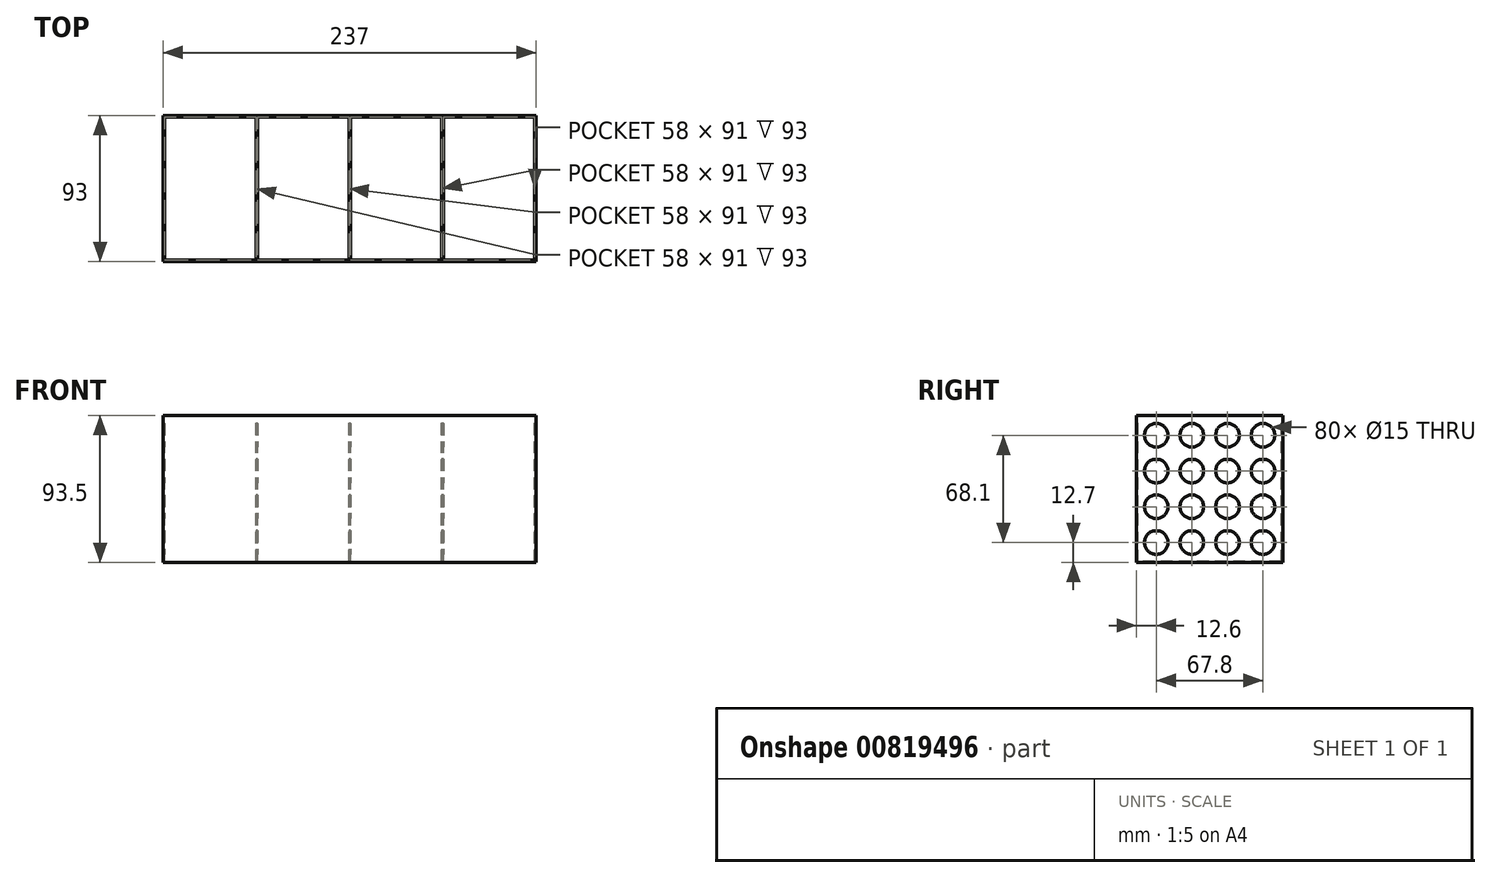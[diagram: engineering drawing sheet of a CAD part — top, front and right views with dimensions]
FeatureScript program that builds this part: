
annotation { "Feature Type Name" : "Feature", "Feature Type Description" : "" }
export const myFeature = defineFeature(function(context is Context, id is Id, definition is map)
    precondition{}
    {
        {
            var Q0;
            Q0=qCreatedBy(makeId("Top.planeOp"),FACE);
            var sketch = newSketch(context, id + "F0", { "sketchPlane" : qUnion([Q0])});
            skLineSegment(sketch, "E0.bottom", {"start": v(-118.5, 46.5) * mm, "end": v(118.5, 46.5) * mm});
            skLineSegment(sketch, "E0.top", {"start": v(-118.5, -46.5) * mm, "end": v(118.5, -46.5) * mm});
            skLineSegment(sketch, "E0.left", {"start": v(-118.5, 46.5) * mm, "end": v(-118.5, -46.5) * mm});
            skLineSegment(sketch, "E0.right", {"start": v(118.5, 46.5) * mm, "end": v(118.5, -46.5) * mm});
            skPoint(sketch, "E0.middle", {"position": v(0, 0) * mm});
            skSolve(sketch);
        }
        {
            var Q0;
            Q0=makeQuery(id+"F0.imprint","IMPRINT",FACE,{"disambiguationData":[TD([[makeQuery(id+"F0.imprint","IMPRINT",EDGE,{"derivedFrom":sQuery(id+"F0.wireOp",EDGE,"E0.bottom")}),-1.0]])]});
            extrude(context, id + "F1", {"entities" : qUnion([Q0]), "depth" : 93.5 * mm, "offsetDistance" : 25 * mm});
        }
        {
            var Q0;
            Q0=makeQuery(id+"F1.opExtrude","CAP_FACE",FACE,{"disambiguationData":[OSD([sQuery(id+"F0.wireOp",EDGE,"E0.bottom"),sQuery(id+"F0.wireOp",EDGE,"E0.top"),sQuery(id+"F0.wireOp",EDGE,"E0.left"),sQuery(id+"F0.wireOp",EDGE,"E0.right")])],"isStart":false});
            var sketch = newSketch(context, id + "F2", { "sketchPlane" : qUnion([Q0])});
            skLineSegment(sketch, "E1.bottom", {"start": v(-117.5, 45.5) * mm, "end": v(-59.5, 45.5) * mm});
            skLineSegment(sketch, "E1.top", {"start": v(-117.5, -45.5) * mm, "end": v(-59.5, -45.5) * mm});
            skLineSegment(sketch, "E1.left", {"start": v(-117.5, 45.5) * mm, "end": v(-117.5, -45.5) * mm});
            skLineSegment(sketch, "E1.right", {"start": v(-59.5, 45.5) * mm, "end": v(-59.5, -45.5) * mm});
            skLineSegment(sketch, "E2", {"start": v(-59.5, 45.5) * mm, "end": v(-58.5, 45.5) * mm});
            skLineSegment(sketch, "E3.bottom", {"start": v(-58.5, 45.5) * mm, "end": v(-0.5, 45.5) * mm});
            skLineSegment(sketch, "E3.top", {"start": v(-58.5, -45.5) * mm, "end": v(-0.5, -45.5) * mm});
            skLineSegment(sketch, "E3.left", {"start": v(-58.5, 45.5) * mm, "end": v(-58.5, -45.5) * mm});
            skLineSegment(sketch, "E3.right", {"start": v(-0.5, 45.5) * mm, "end": v(-0.5, -45.5) * mm});
            skLineSegment(sketch, "E4", {"start": v(-0.5, 45.5) * mm, "end": v(0.5, 45.5) * mm});
            skLineSegment(sketch, "E5.bottom", {"start": v(0.5, 45.5) * mm, "end": v(58.5, 45.5) * mm});
            skLineSegment(sketch, "E5.top", {"start": v(0.5, -45.5) * mm, "end": v(58.5, -45.5) * mm});
            skLineSegment(sketch, "E5.left", {"start": v(0.5, 45.5) * mm, "end": v(0.5, -45.5) * mm});
            skLineSegment(sketch, "E5.right", {"start": v(58.5, 45.5) * mm, "end": v(58.5, -45.5) * mm});
            skLineSegment(sketch, "E6", {"start": v(58.5, 45.5) * mm, "end": v(59.5, 45.5) * mm});
            skLineSegment(sketch, "E7.bottom", {"start": v(59.5, 45.5) * mm, "end": v(117.5, 45.5) * mm});
            skLineSegment(sketch, "E7.top", {"start": v(59.5, -45.5) * mm, "end": v(117.5, -45.5) * mm});
            skLineSegment(sketch, "E7.left", {"start": v(59.5, 45.5) * mm, "end": v(59.5, -45.5) * mm});
            skLineSegment(sketch, "E7.right", {"start": v(117.5, 45.5) * mm, "end": v(117.5, -45.5) * mm});
            skSolve(sketch);
        }
        {
            var Q0;
            Q0 = qSketchRegion(id + "F2", true);
            extrude(context, id + "F3", {"entities" : qUnion([Q0]), "operationType" : NewBodyOperationType.REMOVE, "oppositeDirection" : true, "depth" : 93 * mm, "offsetDistance" : 25 * mm});
        }
        {
            var Q0;
            Q0=makeQuery(id+"F1.opExtrude","SWEPT_FACE",FACE,{"disambiguationData":[OSD([sQuery(id+"F0.wireOp",EDGE,"E0.left")])]});
            var sketch = newSketch(context, id + "F4", { "sketchPlane" : qUnion([Q0])});
            skLineSegment(sketch, "E8", {"start": v(-46.5, 0) * mm, "end": v(-33.9, 0) * mm});
            skLineSegment(sketch, "E9", {"start": v(-33.9, 0) * mm, "end": v(-33.9, 12.7) * mm});
            skCircle(sketch, "E10", {"center": v(-33.9, 12.7) * mm, "radius": 7.5 * mm});
            skLineSegment(sketch, "E11", {"start": v(-33.9, 0) * mm, "end": v(-11.3, 0) * mm});
            skLineSegment(sketch, "E12", {"start": v(-11.3, 0) * mm, "end": v(-11.3, 12.7) * mm});
            skCircle(sketch, "E13", {"center": v(-11.3, 12.7) * mm, "radius": 7.5 * mm});
            skLineSegment(sketch, "E14", {"start": v(-11.3, 0) * mm, "end": v(11.3, 0) * mm});
            skLineSegment(sketch, "E15", {"start": v(11.3, 0) * mm, "end": v(11.3, 12.7) * mm});
            skCircle(sketch, "E16", {"center": v(11.3, 12.7) * mm, "radius": 7.5 * mm});
            skLineSegment(sketch, "E17", {"start": v(11.3, 0) * mm, "end": v(33.9, 0) * mm});
            skLineSegment(sketch, "E18", {"start": v(33.9, 0) * mm, "end": v(33.9, 12.7) * mm});
            skCircle(sketch, "E19", {"center": v(33.9, 12.7) * mm, "radius": 7.5 * mm});
            skLineSegment(sketch, "E20", {"start": v(-33.9, 12.7) * mm, "end": v(-33.9, 35.4) * mm});
            skCircle(sketch, "E21", {"center": v(-33.9, 35.4) * mm, "radius": 7.5 * mm});
            skLineSegment(sketch, "E22", {"start": v(-11.3, 12.7) * mm, "end": v(-11.3, 35.4) * mm});
            skCircle(sketch, "E23", {"center": v(-11.3, 35.4) * mm, "radius": 7.5 * mm});
            skLineSegment(sketch, "E24", {"start": v(11.3, 12.7) * mm, "end": v(11.3, 35.4) * mm});
            skCircle(sketch, "E25", {"center": v(11.3, 35.4) * mm, "radius": 7.5 * mm});
            skLineSegment(sketch, "E26", {"start": v(33.9, 12.7) * mm, "end": v(33.9, 35.4) * mm});
            skCircle(sketch, "E27", {"center": v(33.9, 35.4) * mm, "radius": 7.5 * mm});
            skLineSegment(sketch, "E28", {"start": v(-33.9, 35.4) * mm, "end": v(-33.9, 58.1) * mm});
            skLineSegment(sketch, "E29", {"start": v(-11.3, 35.4) * mm, "end": v(-11.3, 58.1) * mm});
            skLineSegment(sketch, "E30", {"start": v(11.3, 35.4) * mm, "end": v(11.3, 58.1) * mm});
            skLineSegment(sketch, "E31", {"start": v(33.9, 35.4) * mm, "end": v(33.9, 58.1) * mm});
            skLineSegment(sketch, "E32", {"start": v(33.9, 58.1) * mm, "end": v(33.9, 80.8) * mm});
            skLineSegment(sketch, "E33", {"start": v(11.3, 58.1) * mm, "end": v(11.3, 80.8) * mm});
            skLineSegment(sketch, "E34", {"start": v(-11.3, 58.1) * mm, "end": v(-11.3, 80.8) * mm});
            skLineSegment(sketch, "E35", {"start": v(-33.9, 58.1) * mm, "end": v(-33.9, 80.8) * mm});
            skCircle(sketch, "E36", {"center": v(-33.9, 58.1) * mm, "radius": 7.5 * mm});
            skCircle(sketch, "E37", {"center": v(-11.3, 58.1) * mm, "radius": 7.5 * mm});
            skCircle(sketch, "E38", {"center": v(11.3, 58.1) * mm, "radius": 7.5 * mm});
            skCircle(sketch, "E39", {"center": v(33.9, 58.1) * mm, "radius": 7.5 * mm});
            skCircle(sketch, "E40", {"center": v(33.9, 80.8) * mm, "radius": 7.5 * mm});
            skCircle(sketch, "E41", {"center": v(11.3, 80.8) * mm, "radius": 7.5 * mm});
            skCircle(sketch, "E42", {"center": v(-11.3, 80.8) * mm, "radius": 7.5 * mm});
            skCircle(sketch, "E43", {"center": v(-33.9, 80.8) * mm, "radius": 7.5 * mm});
            skSolve(sketch);
        }
        {
            var Q0;
            Q0 = qSketchRegion(id + "F4", true);
            extrude(context, id + "F5", {"entities" : qUnion([Q0]), "operationType" : NewBodyOperationType.REMOVE, "endBound" : BoundingType.THROUGH_ALL, "oppositeDirection" : true, "depth" : 25 * mm, "offsetDistance" : 25 * mm});
        }
    });
